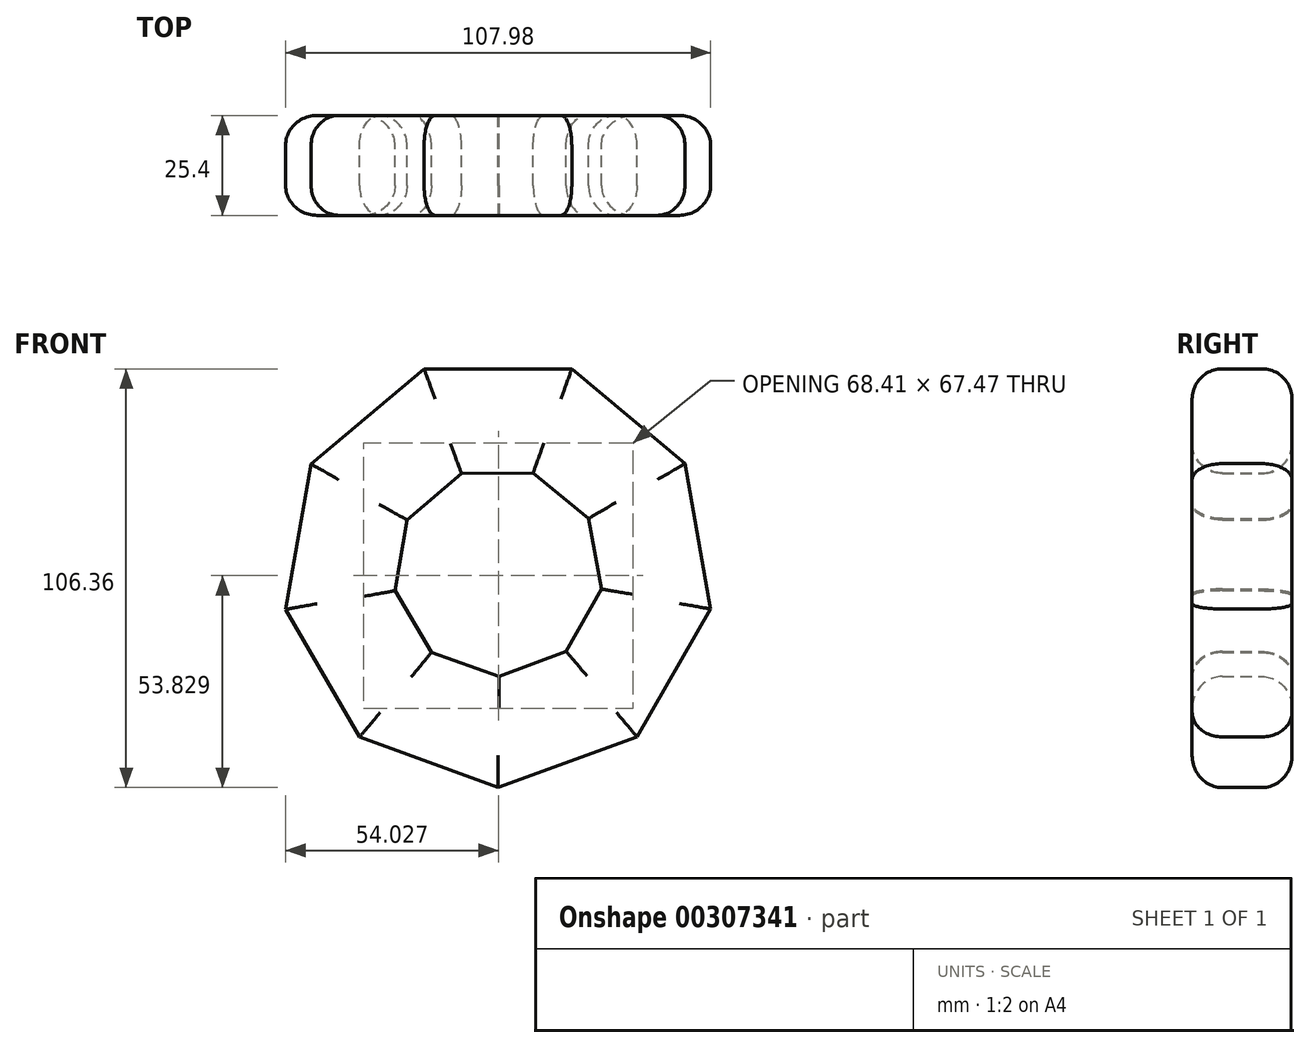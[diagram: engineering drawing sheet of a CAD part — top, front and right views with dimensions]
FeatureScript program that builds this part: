
annotation { "Feature Type Name" : "Feature", "Feature Type Description" : "" }
export const myFeature = defineFeature(function(context is Context, id is Id, definition is map)
    precondition{}
    {
        {
            var Q0;
            Q0=qCreatedBy(makeId("Front.planeOp"),FACE);
            var sketch = newSketch(context, id + "F0", { "sketchPlane" : qUnion([Q0])});
            skCircle(sketch, "E0.cCircle", {"center": v(0, 0) * mm, "radius": 51.52 * mm, "construction": true});
            skLineSegment(sketch, "E0.0", {"start": v(-35.2, -42.03) * mm, "end": v(-53.98, -9.56) * mm});
            skLineSegment(sketch, "E0.1", {"start": v(-53.98, -9.56) * mm, "end": v(-47.5, 27.37) * mm});
            skLineSegment(sketch, "E0.2", {"start": v(-47.5, 27.37) * mm, "end": v(-18.8, 51.5) * mm});
            skLineSegment(sketch, "E0.3", {"start": v(-18.8, 51.5) * mm, "end": v(18.7, 51.53) * mm});
            skLineSegment(sketch, "E0.4", {"start": v(18.7, 51.53) * mm, "end": v(47.46, 27.45) * mm});
            skLineSegment(sketch, "E0.5", {"start": v(47.46, 27.45) * mm, "end": v(54, -9.48) * mm});
            skLineSegment(sketch, "E0.6", {"start": v(54, -9.48) * mm, "end": v(35.27, -41.97) * mm});
            skLineSegment(sketch, "E0.7", {"start": v(35.27, -41.97) * mm, "end": v(0.04, -54.83) * mm});
            skLineSegment(sketch, "E0.8", {"start": v(0.04, -54.83) * mm, "end": v(-35.2, -42.03) * mm});
            skPoint(sketch, "E0.0.midPoint", {"position": v(-44.6, -25.8) * mm});
            skCircle(sketch, "E1.cCircle", {"center": v(0, 0) * mm, "radius": 25.02 * mm, "construction": true});
            skLineSegment(sketch, "E1.0", {"start": v(-16.95, -20.53) * mm, "end": v(-26.18, -4.83) * mm});
            skLineSegment(sketch, "E1.1", {"start": v(-26.18, -4.83) * mm, "end": v(-23.16, 13.13) * mm});
            skLineSegment(sketch, "E1.2", {"start": v(-23.16, 13.13) * mm, "end": v(-9.3, 24.95) * mm});
            skLineSegment(sketch, "E1.3", {"start": v(-9.3, 24.95) * mm, "end": v(8.91, 25.1) * mm});
            skLineSegment(sketch, "E1.4", {"start": v(8.91, 25.1) * mm, "end": v(22.95, 13.5) * mm});
            skLineSegment(sketch, "E1.5", {"start": v(22.95, 13.5) * mm, "end": v(26.26, -4.42) * mm});
            skLineSegment(sketch, "E1.6", {"start": v(26.26, -4.42) * mm, "end": v(17.27, -20.26) * mm});
            skLineSegment(sketch, "E1.7", {"start": v(17.27, -20.26) * mm, "end": v(0.2, -26.62) * mm});
            skLineSegment(sketch, "E1.8", {"start": v(0.2, -26.62) * mm, "end": v(-16.95, -20.53) * mm});
            skPoint(sketch, "E1.0.midPoint", {"position": v(-21.57, -12.68) * mm});
            skSolve(sketch);
        }
        {
            var Q0;
            Q0=makeQuery(id+"F0.imprint","IMPRINT",FACE,{"disambiguationData":[TD([[makeQuery(id+"F0.imprint","IMPRINT",EDGE,{"derivedFrom":sQuery(id+"F0.wireOp",EDGE,"E0.0")}),-1.0]])]});
            extrude(context, id + "F1", {"entities" : qUnion([Q0]), "depth" : 25.4 * mm});
        }
        {
            var Q0;
            Q0=makeQuery(id+"F1.opExtrude","CAP_EDGE",EDGE,{"disambiguationData":[OSD([sQuery(id+"F0.wireOp",EDGE,"E0.3")])],"isStart":true});
            var Q1;
            Q1=makeQuery(id+"F1.opExtrude","CAP_EDGE",EDGE,{"disambiguationData":[OSD([sQuery(id+"F0.wireOp",EDGE,"E0.2")])],"isStart":true});
            var Q2;
            Q2=makeQuery(id+"F1.opExtrude","CAP_EDGE",EDGE,{"disambiguationData":[OSD([sQuery(id+"F0.wireOp",EDGE,"E0.1")])],"isStart":true});
            var Q3;
            Q3=makeQuery(id+"F1.opExtrude","CAP_EDGE",EDGE,{"disambiguationData":[OSD([sQuery(id+"F0.wireOp",EDGE,"E0.0")])],"isStart":true});
            var Q4;
            Q4=makeQuery(id+"F1.opExtrude","CAP_EDGE",EDGE,{"disambiguationData":[OSD([sQuery(id+"F0.wireOp",EDGE,"E0.8")])],"isStart":true});
            var Q5;
            Q5=makeQuery(id+"F1.opExtrude","CAP_EDGE",EDGE,{"disambiguationData":[OSD([sQuery(id+"F0.wireOp",EDGE,"E0.7")])],"isStart":true});
            var Q6;
            Q6=makeQuery(id+"F1.opExtrude","CAP_EDGE",EDGE,{"disambiguationData":[OSD([sQuery(id+"F0.wireOp",EDGE,"E0.6")])],"isStart":true});
            var Q7;
            Q7=makeQuery(id+"F1.opExtrude","CAP_EDGE",EDGE,{"disambiguationData":[OSD([sQuery(id+"F0.wireOp",EDGE,"E0.5")])],"isStart":true});
            var Q8;
            Q8=makeQuery(id+"F1.opExtrude","CAP_EDGE",EDGE,{"disambiguationData":[OSD([sQuery(id+"F0.wireOp",EDGE,"E0.4")])],"isStart":true});
            var Q9;
            Q9=makeQuery(id+"F1.opExtrude","CAP_EDGE",EDGE,{"disambiguationData":[OSD([sQuery(id+"F0.wireOp",EDGE,"E0.2")])],"isStart":false});
            var Q10;
            Q10=makeQuery(id+"F1.opExtrude","CAP_EDGE",EDGE,{"disambiguationData":[OSD([sQuery(id+"F0.wireOp",EDGE,"E0.3")])],"isStart":false});
            var Q11;
            Q11=makeQuery(id+"F1.opExtrude","CAP_EDGE",EDGE,{"disambiguationData":[OSD([sQuery(id+"F0.wireOp",EDGE,"E0.4")])],"isStart":false});
            var Q12;
            Q12=makeQuery(id+"F1.opExtrude","CAP_EDGE",EDGE,{"disambiguationData":[OSD([sQuery(id+"F0.wireOp",EDGE,"E0.5")])],"isStart":false});
            var Q13;
            Q13=makeQuery(id+"F1.opExtrude","CAP_EDGE",EDGE,{"disambiguationData":[OSD([sQuery(id+"F0.wireOp",EDGE,"E0.6")])],"isStart":false});
            var Q14;
            Q14=makeQuery(id+"F1.opExtrude","CAP_EDGE",EDGE,{"disambiguationData":[OSD([sQuery(id+"F0.wireOp",EDGE,"E0.7")])],"isStart":false});
            var Q15;
            Q15=makeQuery(id+"F1.opExtrude","CAP_EDGE",EDGE,{"disambiguationData":[OSD([sQuery(id+"F0.wireOp",EDGE,"E0.8")])],"isStart":false});
            var Q16;
            Q16=makeQuery(id+"F1.opExtrude","CAP_EDGE",EDGE,{"disambiguationData":[OSD([sQuery(id+"F0.wireOp",EDGE,"E0.0")])],"isStart":false});
            var Q17;
            Q17=makeQuery(id+"F1.opExtrude","CAP_EDGE",EDGE,{"disambiguationData":[OSD([sQuery(id+"F0.wireOp",EDGE,"E0.1")])],"isStart":false});
            fillet(context, id + "F2", {"entities" : qUnion([Q0, Q1, Q2, Q3, Q4, Q5, Q6, Q7, Q8, Q9, Q10, Q11, Q12, Q13, Q14, Q15, Q16, Q17]), "radius" : 7.62 * mm, "tangentPropagation" : true, "allowEdgeOverflow" : false});
        }
        {
            var Q0;
            Q0=makeQuery(id+"F1.opExtrude","CAP_EDGE",EDGE,{"disambiguationData":[OSD([sQuery(id+"F0.wireOp",EDGE,"E1.4")])],"isStart":false});
            var Q1;
            Q1=makeQuery(id+"F1.opExtrude","CAP_EDGE",EDGE,{"disambiguationData":[OSD([sQuery(id+"F0.wireOp",EDGE,"E1.5")])],"isStart":false});
            var Q2;
            Q2=makeQuery(id+"F1.opExtrude","CAP_EDGE",EDGE,{"disambiguationData":[OSD([sQuery(id+"F0.wireOp",EDGE,"E1.6")])],"isStart":false});
            var Q3;
            Q3=makeQuery(id+"F1.opExtrude","CAP_EDGE",EDGE,{"disambiguationData":[OSD([sQuery(id+"F0.wireOp",EDGE,"E1.7")])],"isStart":false});
            var Q4;
            Q4=makeQuery(id+"F1.opExtrude","CAP_EDGE",EDGE,{"disambiguationData":[OSD([sQuery(id+"F0.wireOp",EDGE,"E1.8")])],"isStart":false});
            var Q5;
            Q5=makeQuery(id+"F1.opExtrude","CAP_EDGE",EDGE,{"disambiguationData":[OSD([sQuery(id+"F0.wireOp",EDGE,"E1.0")])],"isStart":false});
            var Q6;
            Q6=makeQuery(id+"F1.opExtrude","CAP_EDGE",EDGE,{"disambiguationData":[OSD([sQuery(id+"F0.wireOp",EDGE,"E1.1")])],"isStart":false});
            var Q7;
            Q7=makeQuery(id+"F1.opExtrude","CAP_EDGE",EDGE,{"disambiguationData":[OSD([sQuery(id+"F0.wireOp",EDGE,"E1.2")])],"isStart":false});
            var Q8;
            Q8=makeQuery(id+"F1.opExtrude","CAP_EDGE",EDGE,{"disambiguationData":[OSD([sQuery(id+"F0.wireOp",EDGE,"E1.3")])],"isStart":false});
            var Q9;
            Q9=makeQuery(id+"F1.opExtrude","CAP_EDGE",EDGE,{"disambiguationData":[OSD([sQuery(id+"F0.wireOp",EDGE,"E1.8")])],"isStart":true});
            var Q10;
            Q10=makeQuery(id+"F1.opExtrude","CAP_EDGE",EDGE,{"disambiguationData":[OSD([sQuery(id+"F0.wireOp",EDGE,"E1.7")])],"isStart":true});
            var Q11;
            Q11=makeQuery(id+"F1.opExtrude","CAP_EDGE",EDGE,{"disambiguationData":[OSD([sQuery(id+"F0.wireOp",EDGE,"E1.6")])],"isStart":true});
            var Q12;
            Q12=makeQuery(id+"F1.opExtrude","CAP_EDGE",EDGE,{"disambiguationData":[OSD([sQuery(id+"F0.wireOp",EDGE,"E1.5")])],"isStart":true});
            var Q13;
            Q13=makeQuery(id+"F1.opExtrude","CAP_EDGE",EDGE,{"disambiguationData":[OSD([sQuery(id+"F0.wireOp",EDGE,"E1.4")])],"isStart":true});
            var Q14;
            Q14=makeQuery(id+"F1.opExtrude","CAP_EDGE",EDGE,{"disambiguationData":[OSD([sQuery(id+"F0.wireOp",EDGE,"E1.3")])],"isStart":true});
            var Q15;
            Q15=makeQuery(id+"F1.opExtrude","CAP_EDGE",EDGE,{"disambiguationData":[OSD([sQuery(id+"F0.wireOp",EDGE,"E1.2")])],"isStart":true});
            var Q16;
            Q16=makeQuery(id+"F1.opExtrude","CAP_EDGE",EDGE,{"disambiguationData":[OSD([sQuery(id+"F0.wireOp",EDGE,"E1.1")])],"isStart":true});
            var Q17;
            Q17=makeQuery(id+"F1.opExtrude","CAP_EDGE",EDGE,{"disambiguationData":[OSD([sQuery(id+"F0.wireOp",EDGE,"E1.0")])],"isStart":true});
            fillet(context, id + "F3", {"entities" : qUnion([Q0, Q1, Q2, Q3, Q4, Q5, Q6, Q7, Q8, Q9, Q10, Q11, Q12, Q13, Q14, Q15, Q16, Q17]), "radius" : 7.62 * mm, "tangentPropagation" : true, "allowEdgeOverflow" : false});
        }
    });
